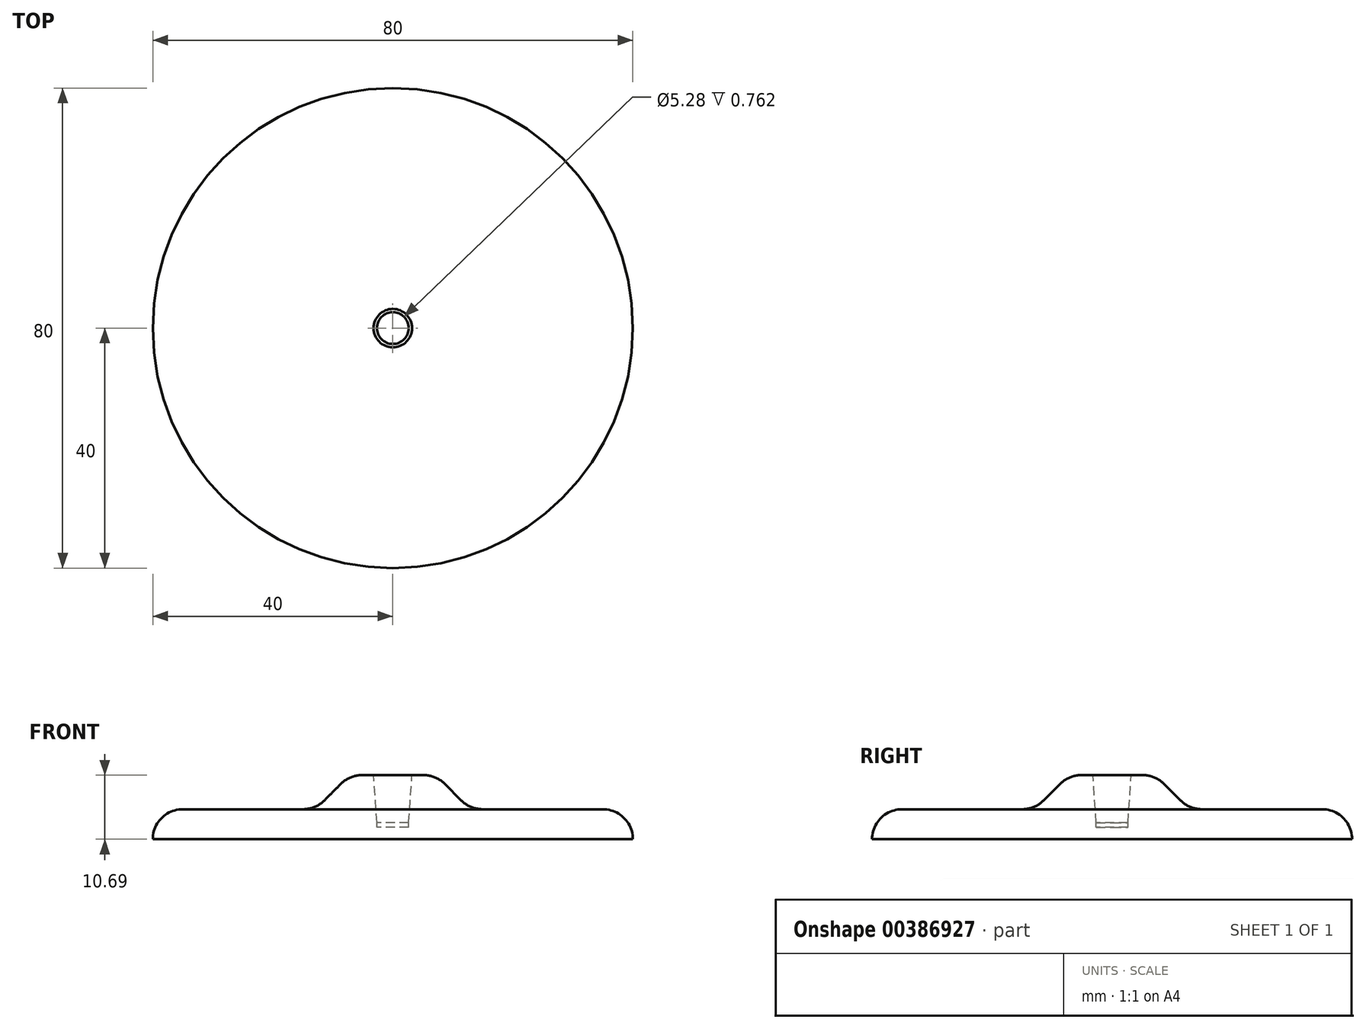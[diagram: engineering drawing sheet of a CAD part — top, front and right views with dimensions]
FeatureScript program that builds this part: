
annotation { "Feature Type Name" : "Feature", "Feature Type Description" : "" }
export const myFeature = defineFeature(function(context is Context, id is Id, definition is map)
    precondition{}
    {
        {
            var Q0;
            Q0=qCreatedBy(makeId("Front.planeOp"),FACE);
            var sketch = newSketch(context, id + "F0", { "sketchPlane" : qUnion([Q0])});
            skLineSegment(sketch, "E0", {"start": v(12.88, 5) * mm, "end": v(40, 5) * mm});
            skLineSegment(sketch, "E1", {"start": v(40, 5) * mm, "end": v(40, 0) * mm});
            skLineSegment(sketch, "E2", {"start": v(40, 0) * mm, "end": v(0, 0) * mm});
            skLineSegment(sketch, "E3", {"start": v(0, 0) * mm, "end": v(0, -22.26) * mm, "construction": true});
            skLineSegment(sketch, "E4", {"start": v(0, 0) * mm, "end": v(0, 2) * mm});
            skLineSegment(sketch, "E5", {"start": v(0, 2) * mm, "end": v(2.64, 2) * mm});
            skLineSegment(sketch, "E6", {"start": v(2.64, 2) * mm, "end": v(2.64, 2.76) * mm});
            skLineSegment(sketch, "E7", {"start": v(2.64, 2.76) * mm, "end": v(3.2, 10.69) * mm});
            skLineSegment(sketch, "E8", {"start": v(3.2, 10.69) * mm, "end": v(7.2, 10.69) * mm});
            skLineSegment(sketch, "E9", {"start": v(7.2, 10.69) * mm, "end": v(12.88, 5) * mm});
            skSolve(sketch);
        }
        {
            var Q0;
            Q0=makeQuery(id+"F0.imprint","IMPRINT",FACE,{"disambiguationData":[TD([[makeQuery(id+"F0.imprint","IMPRINT",EDGE,{"derivedFrom":sQuery(id+"F0.wireOp",EDGE,"E0")}),-1.0]])]});
            var Q1;
            Q1=sQuery(id+"F0.wireOp",EDGE,"E3");
            revolve(context, id + "F1", {"surfaceOperationType" : NewSurfaceOperationType.NEW, "entities" : qUnion([Q0]), "axis" : qUnion([Q1]), "revolveType" : RevolveType.FULL});
        }
        {
            var Q0;
            Q0=makeQuery(id+"F1.opRevolve","SWEPT_EDGE",EDGE,{"disambiguationData":[OSD([sQuery(id+"F0.wireOp",EDGE,"E0"),sQuery(id+"F0.wireOp",EDGE,"E9")])]});
            var Q1;
            Q1=makeQuery(id+"F1.opRevolve","SWEPT_EDGE",EDGE,{"disambiguationData":[OSD([sQuery(id+"F0.wireOp",EDGE,"E0"),sQuery(id+"F0.wireOp",EDGE,"E1")])]});
            var Q2;
            Q2=makeQuery(id+"F1.opRevolve","SWEPT_EDGE",EDGE,{"disambiguationData":[OSD([sQuery(id+"F0.wireOp",EDGE,"E8"),sQuery(id+"F0.wireOp",EDGE,"E9")])]});
            fillet(context, id + "F2", {"entities" : qUnion([Q0, Q1, Q2]), "radius" : 5 * mm, "tangentPropagation" : true, "allowEdgeOverflow" : false});
        }
    });
